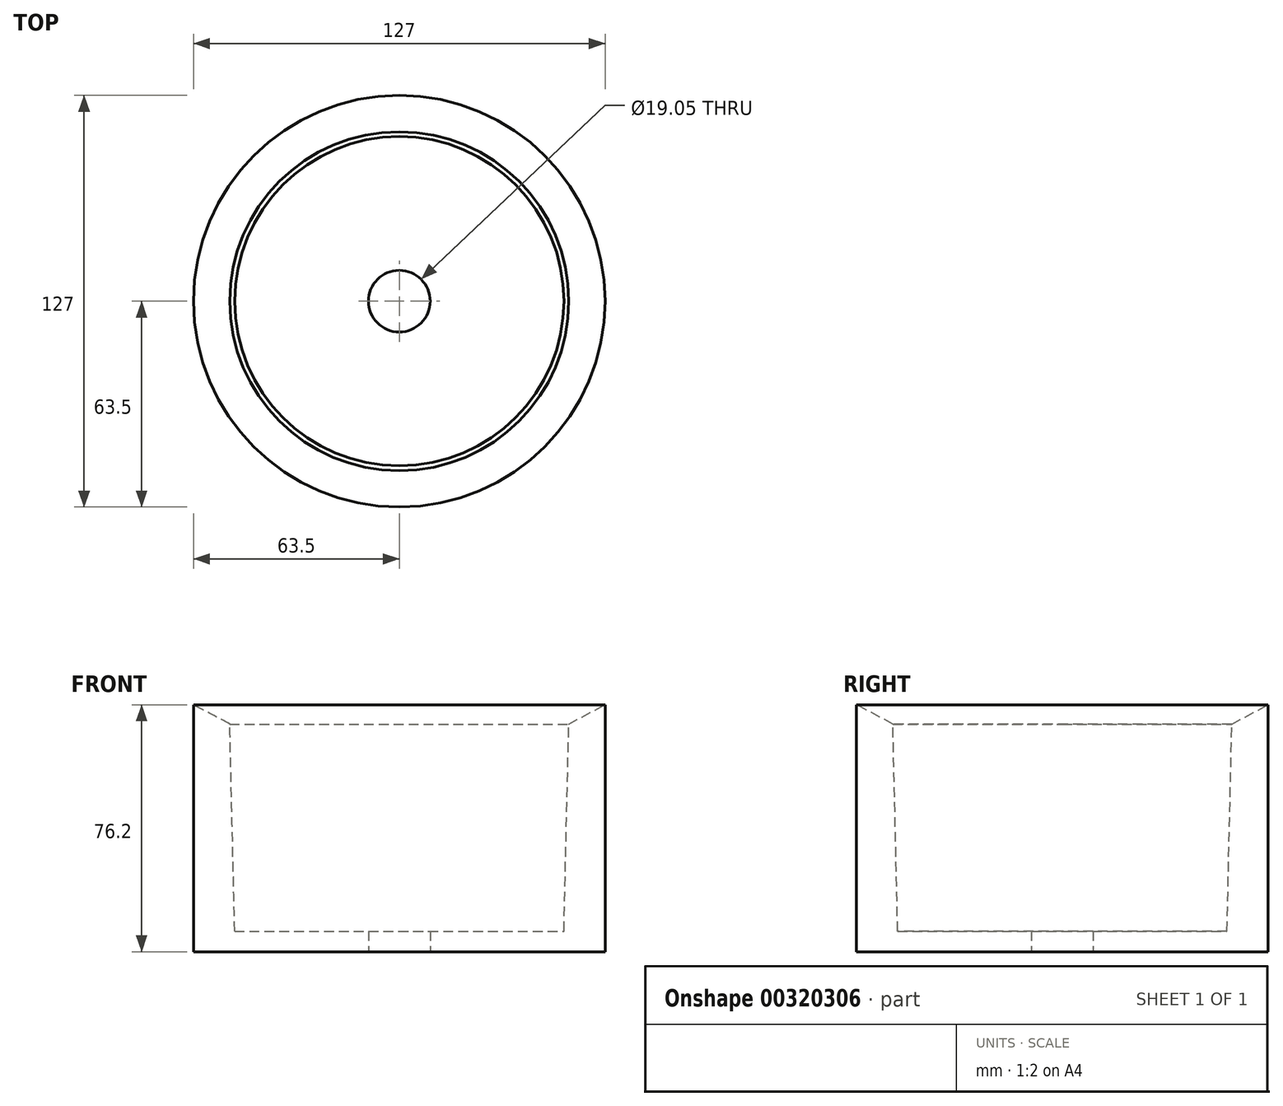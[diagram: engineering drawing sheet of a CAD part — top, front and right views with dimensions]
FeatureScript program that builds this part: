
annotation { "Feature Type Name" : "Feature", "Feature Type Description" : "" }
export const myFeature = defineFeature(function(context is Context, id is Id, definition is map)
    precondition{}
    {
        {
            var Q0;
            Q0=qCreatedBy(makeId("Front.planeOp"),FACE);
            var sketch = newSketch(context, id + "F0", { "sketchPlane" : qUnion([Q0])});
            skLineSegment(sketch, "E0", {"start": v(0, 0) * mm, "end": v(0, 70.89) * mm, "construction": true});
            skLineSegment(sketch, "E1", {"start": v(99.2, 0) * mm, "end": v(0, 0) * mm, "construction": true});
            skSolve(sketch);
        }
        {
            var Q0;
            Q0=qCreatedBy(makeId("Front.planeOp"),FACE);
            var sketch = newSketch(context, id + "F1", { "sketchPlane" : qUnion([Q0])});
            skLineSegment(sketch, "E2", {"start": v(-63.5, 76.2) * mm, "end": v(-63.5, 0) * mm});
            skLineSegment(sketch, "E3", {"start": v(-63.5, 0) * mm, "end": v(0, 0) * mm});
            skLineSegment(sketch, "E4", {"start": v(0, 0) * mm, "end": v(0, 6.35) * mm});
            skLineSegment(sketch, "E5", {"start": v(0, 6.35) * mm, "end": v(-50.8, 6.35) * mm});
            skLineSegment(sketch, "E6", {"start": v(-50.8, 6.35) * mm, "end": v(-52.28, 70.24) * mm});
            skLineSegment(sketch, "E7", {"start": v(-52.28, 70.24) * mm, "end": v(-63.5, 76.2) * mm});
            skSolve(sketch);
        }
        {
            var Q0;
            Q0=makeQuery(id+"F1.imprint","IMPRINT",FACE,{"disambiguationData":[TD([[makeQuery(id+"F1.imprint","IMPRINT",EDGE,{"derivedFrom":sQuery(id+"F1.wireOp",EDGE,"E2")}),1.0]])]});
            var Q1;
            Q1=sQuery(id+"F0.wireOp",EDGE,"E0");
            revolve(context, id + "F2", {"entities" : qUnion([Q0]), "axis" : qUnion([Q1]), "revolveType" : RevolveType.FULL});
        }
        {
            var Q0;
            Q0=makeQuery(id+"F2.opRevolve","SWEPT_FACE",FACE,{"disambiguationData":[OSD([sQuery(id+"F1.wireOp",EDGE,"E3")])]});
            var sketch = newSketch(context, id + "F3", { "sketchPlane" : qUnion([Q0])});
            skCircle(sketch, "E8", {"center": v(0, 0) * mm, "radius": 9.53 * mm});
            skSolve(sketch);
        }
        {
            var Q0;
            Q0 = qSketchRegion(id + "F3", true);
            extrude(context, id + "F4", {"entities" : qUnion([Q0]), "operationType" : NewBodyOperationType.REMOVE, "endBound" : BoundingType.THROUGH_ALL, "oppositeDirection" : true, "depth" : 25.4 * mm});
        }
    });
